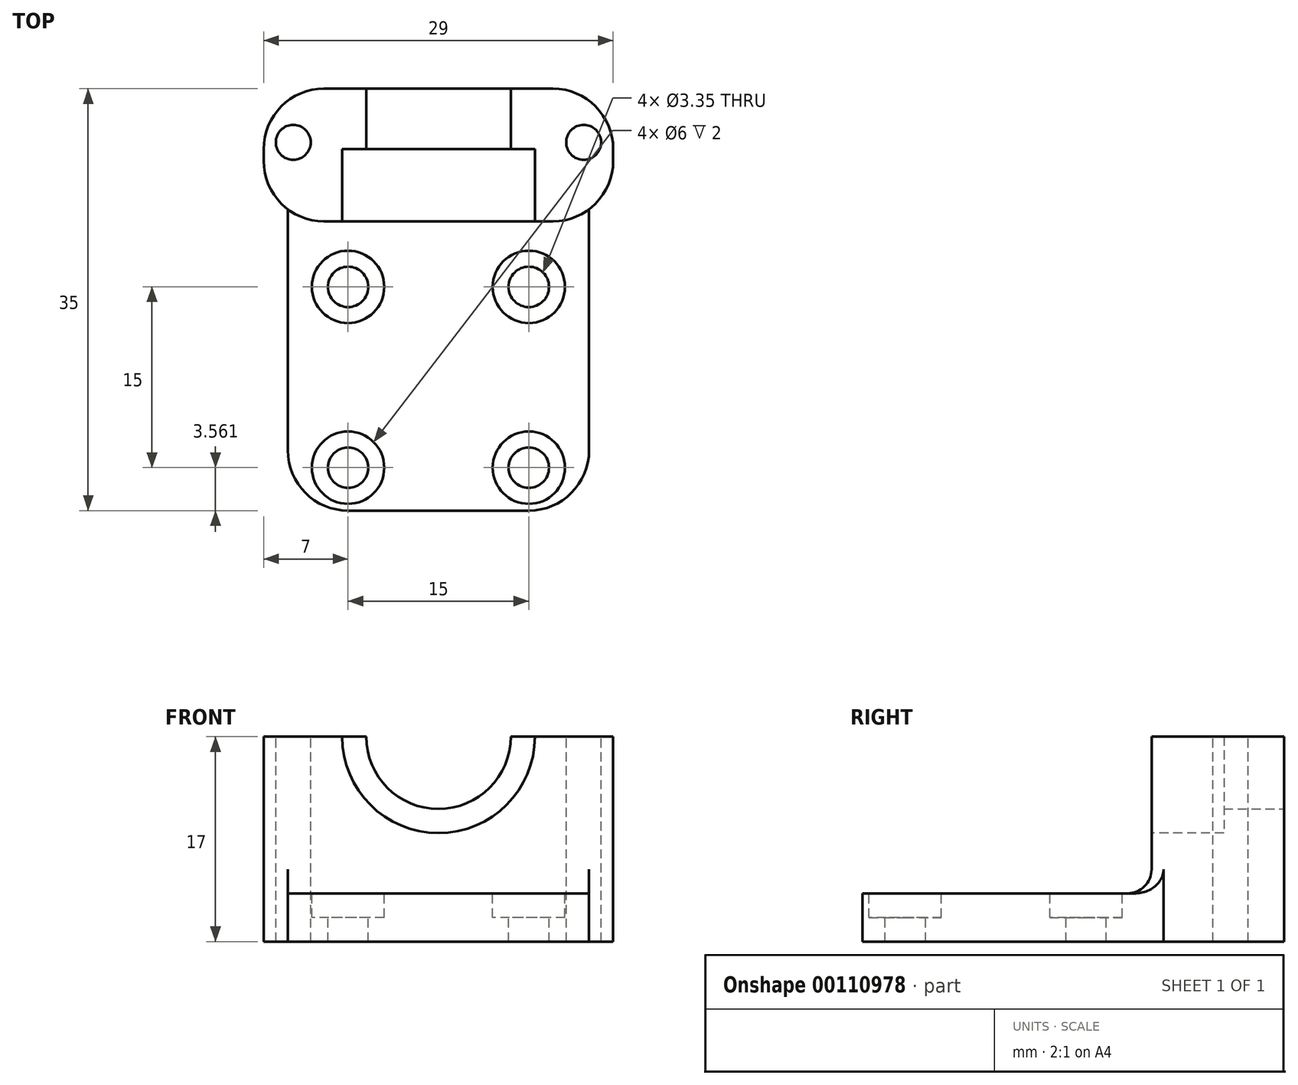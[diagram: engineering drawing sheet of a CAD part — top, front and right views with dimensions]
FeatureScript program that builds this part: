
annotation { "Feature Type Name" : "Feature", "Feature Type Description" : "" }
export const myFeature = defineFeature(function(context is Context, id is Id, definition is map)
    precondition{}
    {
        {
            var Q0;
            Q0=qCreatedBy(makeId("Top.planeOp"),FACE);
            var sketch = newSketch(context, id + "F0", { "sketchPlane" : qUnion([Q0])});
            skLineSegment(sketch, "E0.bottom", {"start": v(0, 0) * mm, "end": v(25, 0) * mm});
            skLineSegment(sketch, "E0.top", {"start": v(0, 35) * mm, "end": v(25, 35) * mm});
            skLineSegment(sketch, "E0.left", {"start": v(0, 0) * mm, "end": v(0, 35) * mm});
            skLineSegment(sketch, "E0.right", {"start": v(25, 0) * mm, "end": v(25, 35) * mm});
            skSolve(sketch);
        }
        {
            var Q0;
            Q0=qSketchRegion(id+"F0",true);
            extrude(context, id + "F1", {"entities" : qUnion([Q0]), "depth" : 4 * mm});
        }
        {
            var Q0;
            Q0=makeQuery(id+"F1.opExtrude","CAP_FACE",FACE,{"disambiguationData":[OSD([sQuery(id+"F0.wireOp",EDGE,"E0.bottom"),sQuery(id+"F0.wireOp",EDGE,"E0.top"),sQuery(id+"F0.wireOp",EDGE,"E0.left"),sQuery(id+"F0.wireOp",EDGE,"E0.right")])],"isStart":false});
            var sketch = newSketch(context, id + "F2", { "sketchPlane" : qUnion([Q0])});
            skCircle(sketch, "E1", {"center": v(5, 18.56) * mm, "radius": 1.68 * mm});
            skCircle(sketch, "E2", {"center": v(20, 18.56) * mm, "radius": 1.68 * mm});
            skCircle(sketch, "E3", {"center": v(5, 3.56) * mm, "radius": 1.68 * mm});
            skCircle(sketch, "E4", {"center": v(20, 3.56) * mm, "radius": 1.68 * mm});
            skLineSegment(sketch, "E5", {"start": v(5, 18.56) * mm, "end": v(0, 18.56) * mm});
            skLineSegment(sketch, "E6", {"start": v(20, 3.56) * mm, "end": v(25, 3.56) * mm});
            skCircle(sketch, "E7", {"center": v(5, 18.56) * mm, "radius": 3 * mm});
            skCircle(sketch, "E8", {"center": v(20, 18.56) * mm, "radius": 3 * mm});
            skCircle(sketch, "E9", {"center": v(5, 3.56) * mm, "radius": 3 * mm});
            skCircle(sketch, "E10", {"center": v(20, 3.56) * mm, "radius": 3 * mm});
            skSolve(sketch);
        }
        {
            var Q0;
            Q0=makeQuery(id+"F2.imprint","IMPRINT",FACE,{"disambiguationData":[TD([[makeQuery(id+"F2.imprint","IMPRINT",EDGE,{"derivedFrom":sQuery(id+"F2.wireOp",EDGE,"E1")}),1.0]])]});
            var Q1;
            Q1=makeQuery(id+"F2.imprint","IMPRINT",FACE,{"disambiguationData":[TD([[makeQuery(id+"F2.imprint","IMPRINT",EDGE,{"derivedFrom":sQuery(id+"F2.wireOp",EDGE,"E2")}),1.0]])]});
            var Q2;
            Q2=makeQuery(id+"F2.imprint","IMPRINT",FACE,{"disambiguationData":[TD([[makeQuery(id+"F2.imprint","IMPRINT",EDGE,{"derivedFrom":sQuery(id+"F2.wireOp",EDGE,"E4")}),1.0]])]});
            var Q3;
            Q3=makeQuery(id+"F2.imprint","IMPRINT",FACE,{"disambiguationData":[TD([[makeQuery(id+"F2.imprint","IMPRINT",EDGE,{"derivedFrom":sQuery(id+"F2.wireOp",EDGE,"E3")}),1.0]])]});
            extrude(context, id + "F3", {"entities" : qUnion([Q0, Q1, Q2, Q3]), "operationType" : NewBodyOperationType.REMOVE, "oppositeDirection" : true, "depth" : 25 * mm});
        }
        {
            var Q0;
            Q0=makeQuery(id+"F1.opExtrude","CAP_FACE",FACE,{"disambiguationData":[OSD([sQuery(id+"F0.wireOp",EDGE,"E0.bottom"),sQuery(id+"F0.wireOp",EDGE,"E0.top"),sQuery(id+"F0.wireOp",EDGE,"E0.left"),sQuery(id+"F0.wireOp",EDGE,"E0.right")])],"isStart":false});
            var sketch = newSketch(context, id + "F4", { "sketchPlane" : qUnion([Q0])});
            skLineSegment(sketch, "E11.bottom", {"start": v(0, 35) * mm, "end": v(25, 35) * mm});
            skLineSegment(sketch, "E11.top", {"start": v(0, 24) * mm, "end": v(25, 24) * mm});
            skLineSegment(sketch, "E11.left", {"start": v(0, 35) * mm, "end": v(0, 24) * mm});
            skLineSegment(sketch, "E11.right", {"start": v(25, 35) * mm, "end": v(25, 24) * mm});
            skSolve(sketch);
        }
        {
            var Q0;
            Q0=qSketchRegion(id+"F4",true);
            extrude(context, id + "F5", {"entities" : qUnion([Q0]), "operationType" : NewBodyOperationType.ADD, "depth" : 13 * mm});
        }
        {
            var Q0;
            Q0=makeQuery(id+"F5.boolean.opBoolean","MERGE",FACE,{"derivedFrom":[makeQuery(id+"F1.opExtrude","SWEPT_FACE",FACE,{"disambiguationData":[OSD([sQuery(id+"F0.wireOp",EDGE,"E0.top")])]}),makeQuery(id+"F5.opExtrude","SWEPT_FACE",FACE,{"disambiguationData":[OSD([sQuery(id+"F4.wireOp",EDGE,"E11.bottom")])]})]});
            var sketch = newSketch(context, id + "F6", { "sketchPlane" : qUnion([Q0])});
            skCircle(sketch, "E12", {"center": v(-12.5, 17) * mm, "radius": 6 * mm});
            skSolve(sketch);
        }
        {
            var Q0;
            {var subQ0=makeQuery(id+"F5.opExtrude","CAP_EDGE",EDGE,{"disambiguationData":[OSD([sQuery(id+"F4.wireOp",EDGE,"E11.bottom")])],"isStart":false});var subQ1=sQuery(id+"F6.wireOp",EDGE,"E12");var subQ3=makeQuery(id+"F6.imprint","INTERSECT",VERTEX,{"disambiguationData":[OD(0.0)],"derivedFrom":[subQ0,subQ1]});Q0=makeQuery(id+"F6.imprint","IMPRINT",FACE,{"disambiguationData":[TD([[makeQuery(id+"F6.imprint","IMPRINT",EDGE,{"disambiguationData":[TD([[subQ3,1.0]])],"derivedFrom":subQ1}),1.0]])]});}
            extrude(context, id + "F7", {"entities" : qUnion([Q0]), "operationType" : NewBodyOperationType.REMOVE, "oppositeDirection" : true, "depth" : 6 * mm});
        }
        {
            var Q0;
            Q0=makeQuery(id+"F5.opExtrude","SWEPT_FACE",FACE,{"disambiguationData":[OSD([sQuery(id+"F4.wireOp",EDGE,"E11.top")])]});
            var sketch = newSketch(context, id + "F8", { "sketchPlane" : qUnion([Q0])});
            skCircle(sketch, "E13", {"center": v(12.5, 17) * mm, "radius": 8 * mm});
            skSolve(sketch);
        }
        {
            var Q0;
            Q0=qSketchRegion(id+"F8",true);
            extrude(context, id + "F9", {"entities" : qUnion([Q0]), "operationType" : NewBodyOperationType.REMOVE, "oppositeDirection" : true, "depth" : 6 * mm});
        }
        {
            var Q0;
            Q0=makeQuery(id+"F2.imprint","IMPRINT",FACE,{"disambiguationData":[TD([[makeQuery(id+"F2.imprint","IMPRINT",EDGE,{"derivedFrom":sQuery(id+"F2.wireOp",EDGE,"E1")}),-1.0]])]});
            var Q1;
            Q1=makeQuery(id+"F2.imprint","IMPRINT",FACE,{"disambiguationData":[TD([[makeQuery(id+"F2.imprint","IMPRINT",EDGE,{"derivedFrom":sQuery(id+"F2.wireOp",EDGE,"E2")}),-1.0]])]});
            var Q2;
            Q2=makeQuery(id+"F2.imprint","IMPRINT",FACE,{"disambiguationData":[TD([[makeQuery(id+"F2.imprint","IMPRINT",EDGE,{"derivedFrom":sQuery(id+"F2.wireOp",EDGE,"E4")}),-1.0]])]});
            var Q3;
            Q3=makeQuery(id+"F2.imprint","IMPRINT",FACE,{"disambiguationData":[TD([[makeQuery(id+"F2.imprint","IMPRINT",EDGE,{"derivedFrom":sQuery(id+"F2.wireOp",EDGE,"E3")}),-1.0]])]});
            extrude(context, id + "F10", {"entities" : qUnion([Q0, Q1, Q2, Q3]), "operationType" : NewBodyOperationType.REMOVE, "oppositeDirection" : true, "depth" : 2 * mm});
        }
        {
            var Q0;
            Q0=makeQuery(id+"F1.opExtrude","SWEPT_EDGE",EDGE,{"disambiguationData":[OSD([sQuery(id+"F0.wireOp",EDGE,"E0.bottom"),sQuery(id+"F0.wireOp",EDGE,"E0.left")])]});
            var Q1;
            Q1=makeQuery(id+"F1.opExtrude","SWEPT_EDGE",EDGE,{"disambiguationData":[OSD([sQuery(id+"F0.wireOp",EDGE,"E0.bottom"),sQuery(id+"F0.wireOp",EDGE,"E0.right")])]});
            fillet(context, id + "F11", {"entities" : qUnion([Q0, Q1]), "radius" : 5 * mm, "tangentPropagation" : true, "allowEdgeOverflow" : false});
        }
        {
            var Q0;
            Q0=makeQuery(id+"F5.boolean.opBoolean","MERGE",FACE,{"derivedFrom":[makeQuery(id+"F1.opExtrude","SWEPT_FACE",FACE,{"disambiguationData":[OSD([sQuery(id+"F0.wireOp",EDGE,"E0.left")])]}),makeQuery(id+"F5.opExtrude","SWEPT_FACE",FACE,{"disambiguationData":[OSD([sQuery(id+"F4.wireOp",EDGE,"E11.left")])]})]});
            var sketch = newSketch(context, id + "F12", { "sketchPlane" : qUnion([Q0])});
            skLineSegment(sketch, "E14.bottom", {"start": v(-35, 0) * mm, "end": v(-24, 0) * mm});
            skLineSegment(sketch, "E14.top", {"start": v(-35, 17) * mm, "end": v(-24, 17) * mm});
            skLineSegment(sketch, "E14.left", {"start": v(-35, 0) * mm, "end": v(-35, 17) * mm});
            skLineSegment(sketch, "E14.right", {"start": v(-24, 0) * mm, "end": v(-24, 17) * mm});
            skSolve(sketch);
        }
        {
            var Q0;
            {var subQ3=sQuery(id+"F12.wireOp",EDGE,"E14.bottom");Q0=makeQuery(id+"F12.imprint","IMPRINT",FACE,{"disambiguationData":[TD([[makeQuery(id+"F12.imprint","IMPRINT",EDGE,{"derivedFrom":subQ3}),-1.0]])]});}
            extrude(context, id + "F13", {"entities" : qUnion([Q0]), "operationType" : NewBodyOperationType.ADD, "depth" : 2 * mm});
        }
        {
            var Q0;
            Q0=makeQuery(id+"F5.boolean.opBoolean","MERGE",FACE,{"derivedFrom":[makeQuery(id+"F1.opExtrude","SWEPT_FACE",FACE,{"disambiguationData":[OSD([sQuery(id+"F0.wireOp",EDGE,"E0.right")])]}),makeQuery(id+"F5.opExtrude","SWEPT_FACE",FACE,{"disambiguationData":[OSD([sQuery(id+"F4.wireOp",EDGE,"E11.right")])]})]});
            var sketch = newSketch(context, id + "F14", { "sketchPlane" : qUnion([Q0])});
            skLineSegment(sketch, "E15.bottom", {"start": v(35, 0) * mm, "end": v(24, 0) * mm});
            skLineSegment(sketch, "E15.top", {"start": v(35, 17) * mm, "end": v(24, 17) * mm});
            skLineSegment(sketch, "E15.left", {"start": v(35, 0) * mm, "end": v(35, 17) * mm});
            skLineSegment(sketch, "E15.right", {"start": v(24, 0) * mm, "end": v(24, 17) * mm});
            skSolve(sketch);
        }
        {
            var Q0;
            Q0=qSketchRegion(id+"F14",true);
            extrude(context, id + "F15", {"entities" : qUnion([Q0]), "operationType" : NewBodyOperationType.ADD, "depth" : 2 * mm});
        }
        {
            var Q0;
            {var subQ0=sQuery(id+"F4.wireOp",EDGE,"E11.bottom");var subQ1=sQuery(id+"F4.wireOp",EDGE,"E11.top");var subQ2=sQuery(id+"F4.wireOp",EDGE,"E11.left");Q0=makeQuery(id+"F9.boolean.opBoolean","SPLIT",FACE,{"disambiguationData":[TD([makeQuery(id+"F1.opExtrude","SWEPT_FACE",FACE,{"disambiguationData":[OSD([sQuery(id+"F0.wireOp",EDGE,"E0.left")])]})])],"derivedFrom":makeQuery(id+"F5.opExtrude","CAP_FACE",FACE,{"disambiguationData":[OSD([subQ0,subQ1,subQ2,sQuery(id+"F4.wireOp",EDGE,"E11.right")])],"isStart":false})});}
            var sketch = newSketch(context, id + "F16", { "sketchPlane" : qUnion([Q0])});
            skCircle(sketch, "E16", {"center": v(0.45, 30.55) * mm, "radius": 1.45 * mm});
            skCircle(sketch, "E17", {"center": v(24.55, 30.55) * mm, "radius": 1.45 * mm});
            skSolve(sketch);
        }
        {
            var Q0;
            Q0=qSketchRegion(id+"F16",true);
            extrude(context, id + "F17", {"entities" : qUnion([Q0]), "operationType" : NewBodyOperationType.REMOVE, "oppositeDirection" : true, "depth" : 25 * mm});
        }
        {
            var Q0;
            Q0=makeQuery(id+"F13.opExtrude","CAP_EDGE",EDGE,{"disambiguationData":[OSD([sQuery(id+"F12.wireOp",EDGE,"E14.right")])],"isStart":false});
            var Q1;
            Q1=makeQuery(id+"F13.opExtrude","CAP_EDGE",EDGE,{"disambiguationData":[OSD([sQuery(id+"F12.wireOp",EDGE,"E14.left")])],"isStart":false});
            var Q2;
            Q2=makeQuery(id+"F15.opExtrude","CAP_EDGE",EDGE,{"disambiguationData":[OSD([sQuery(id+"F14.wireOp",EDGE,"E15.left")])],"isStart":false});
            var Q3;
            Q3=makeQuery(id+"F15.opExtrude","CAP_EDGE",EDGE,{"disambiguationData":[OSD([sQuery(id+"F14.wireOp",EDGE,"E15.right")])],"isStart":false});
            fillet(context, id + "F18", {"entities" : qUnion([Q0, Q1, Q2, Q3]), "radius" : 5 * mm, "tangentPropagation" : true, "allowEdgeOverflow" : false});
        }
        {
            var Q0;
            Q0=makeQuery(id+"F5.opExtrude","CAP_EDGE",EDGE,{"disambiguationData":[OSD([sQuery(id+"F4.wireOp",EDGE,"E11.top")])],"isStart":true});
            var Q1;
            Q1=makeQuery(id+"F18.opFillet","BLEND_EDGE",EDGE,{"blendedFrom":[makeQuery(id+"F15.opExtrude","CAP_EDGE",EDGE,{"disambiguationData":[OSD([sQuery(id+"F14.wireOp",EDGE,"E15.right")])],"isStart":false}),makeQuery(id+"F1.opExtrude","CAP_FACE",FACE,{"disambiguationData":[OSD([sQuery(id+"F0.wireOp",EDGE,"E0.bottom"),sQuery(id+"F0.wireOp",EDGE,"E0.top"),sQuery(id+"F0.wireOp",EDGE,"E0.left"),sQuery(id+"F0.wireOp",EDGE,"E0.right")])],"isStart":false})],"blendedInto":[makeQuery(id+"F1.opExtrude","CAP_FACE",FACE,{"disambiguationData":[OSD([sQuery(id+"F0.wireOp",EDGE,"E0.bottom"),sQuery(id+"F0.wireOp",EDGE,"E0.top"),sQuery(id+"F0.wireOp",EDGE,"E0.left"),sQuery(id+"F0.wireOp",EDGE,"E0.right")])],"isStart":false})]});
            var Q2;
            Q2=makeQuery(id+"F18.opFillet","BLEND_EDGE",EDGE,{"blendedFrom":[makeQuery(id+"F13.opExtrude","CAP_EDGE",EDGE,{"disambiguationData":[OSD([sQuery(id+"F12.wireOp",EDGE,"E14.right")])],"isStart":false}),makeQuery(id+"F1.opExtrude","CAP_FACE",FACE,{"disambiguationData":[OSD([sQuery(id+"F0.wireOp",EDGE,"E0.bottom"),sQuery(id+"F0.wireOp",EDGE,"E0.top"),sQuery(id+"F0.wireOp",EDGE,"E0.left"),sQuery(id+"F0.wireOp",EDGE,"E0.right")])],"isStart":false})],"blendedInto":[makeQuery(id+"F1.opExtrude","CAP_FACE",FACE,{"disambiguationData":[OSD([sQuery(id+"F0.wireOp",EDGE,"E0.bottom"),sQuery(id+"F0.wireOp",EDGE,"E0.top"),sQuery(id+"F0.wireOp",EDGE,"E0.left"),sQuery(id+"F0.wireOp",EDGE,"E0.right")])],"isStart":false})]});
            fillet(context, id + "F19", {"entities" : qUnion([Q0, Q1, Q2]), "radius" : 2 * mm, "tangentPropagation" : true, "allowEdgeOverflow" : false});
        }
    });
